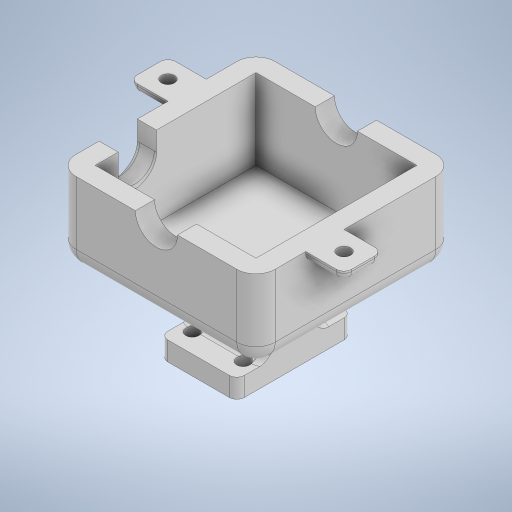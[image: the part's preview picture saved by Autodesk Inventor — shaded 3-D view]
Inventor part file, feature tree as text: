
AUTODESK INVENTOR PART (.ipt)
format: ipt  version: 2023.2 (Build 272271000, 271)  size: 542,720 bytes
history: native  units: mm
features: sketch x16, extrude x11, fillet x10, hole x2, other x1
ambient origin geometry x8: Origin, YZ Plane, XZ Plane, XY Plane, X Axis, Y Axis, Z Axis, Center Point
bodies: Solid1 (feature_tree)
feature tree (40):
  extrude  "Extrusion1"  Depth=30.0mm
  hole  "Hole1"  [1 undecoded]
  extrude  "Extrusion2"  Depth=2.0mm
  sketch  "Sketch4"  dims[d6=5.0mm d7=0.0mm d8=12.0mm]
  extrude  "Extrusion3"  Depth=5.0mm
  extrude  "Extrusion4"  Depth=2.0mm
  sketch  "Sketch7"  dims[d18=15.0mm d19=15.0mm d20=0.0mm]
  sketch  "Sketch8"  dims[d21=15.0mm d22=0.5mm]
  extrude  "Extrusion6"  Depth=15.0mm TaperAngle=0.0deg
  extrude  "Extrusion7"  Depth=0.5mm
  extrude  "Extrusion8"  Depth=15.0mm
  extrude  "Extrusion9"  Depth=16.0mm TaperAngle=0.0deg
  extrude  "Extrusion10"  Depth=5.0mm TaperAngle=0.0deg
  fillet  "Face Fillet1"
  fillet  "Face Fillet2"
  other  "Full Round Fillet1"
  fillet  "Face Fillet9"
  fillet  "Face Fillet10"
  fillet  "Face Fillet11"
  fillet  "Face Fillet12"
  fillet  "Face Fillet13"
  fillet  "Face Fillet14"
  fillet  "Fillet1"  Radius=5.0mm
  extrude  "Extrusion11"  Depth=5.0mm
  extrude  "Extrusion12"  Depth=5.0mm
  hole  "Hole2"  [1 undecoded]
  fillet  "Fillet2"  Radius=5.0mm
  sketch  "Sketch1"  dims[d0=20.0mm d1=30.0mm]
  sketch  "Sketch2"  dims[d2=12.0mm d3=12.0mm]
  sketch  "Sketch3"  dims[d4=9.827949mm d5=2.0mm]
  sketch  "Sketch5"  dims[d9=9.827949mm]
  sketch  "Sketch6"  dims[d10=3.4mm d11=6.0mm d12=6.3mm d13=2.0mm d14=90.0deg d15=8.0mm d16=20.594885mm d17=20.0mm]
  sketch  "Sketch11"  dims[d23=16.0mm d24=0.0mm d25=15.0mm]
  sketch  "Sketch12"  dims[d26=0.5mm d27=16.0mm d28=0.0mm]
  sketch  "Sketch13"  dims[d31=18.5mm d32=0.0mm d33=18.5mm d34=0.0mm d35=5.0mm]
  sketch  "Sketch14"  dims[d36=5.0mm d37=42.0mm]
  sketch  "Sketch15"  dims[d38=42.0mm d39=5.0mm]
  sketch  "Sketch16"  dims[d40=21.0mm d41=0.0mm d42=5.0mm d43=5.0mm]
  sketch  "Sketch17"  dims[d44=21.0mm]
  sketch  "Sketch18"  dims[d45=5.0mm d46=15.0mm d47=20.0mm d49=1.0mm d50=5.0mm d51=10.0mm d52=5.0mm d53=10.0mm d54=5.0mm d55=21.0mm d56=0.0mm d57=1.5mm d58=5.0mm d60=0.0mm d61=0.0mm d62=0.589mm d63=0.589mm d70=5.0mm d71=5.0mm d72=5.0mm d73=5.0mm d74=5.0mm d75=5.0mm d76=2.0mm d77=11.0mm d78=8.0mm d79=10.0mm d80=2.5mm d81=10.0mm d82=0.0mm d83=8.0mm d84=10.0mm d85=2.5mm d86=10.0mm d87=0.0mm d88=3.4mm d89=6.0mm d90=4.0mm d91=2.0mm d92=90.0deg d93=8.0mm d94=20.594885mm d95=2.0mm]
note: 2 required parameter values undecoded (feature->parameter linkage not recoverable at this tier; creation-order binding heuristic only, values carry confidence <= 0.55)
